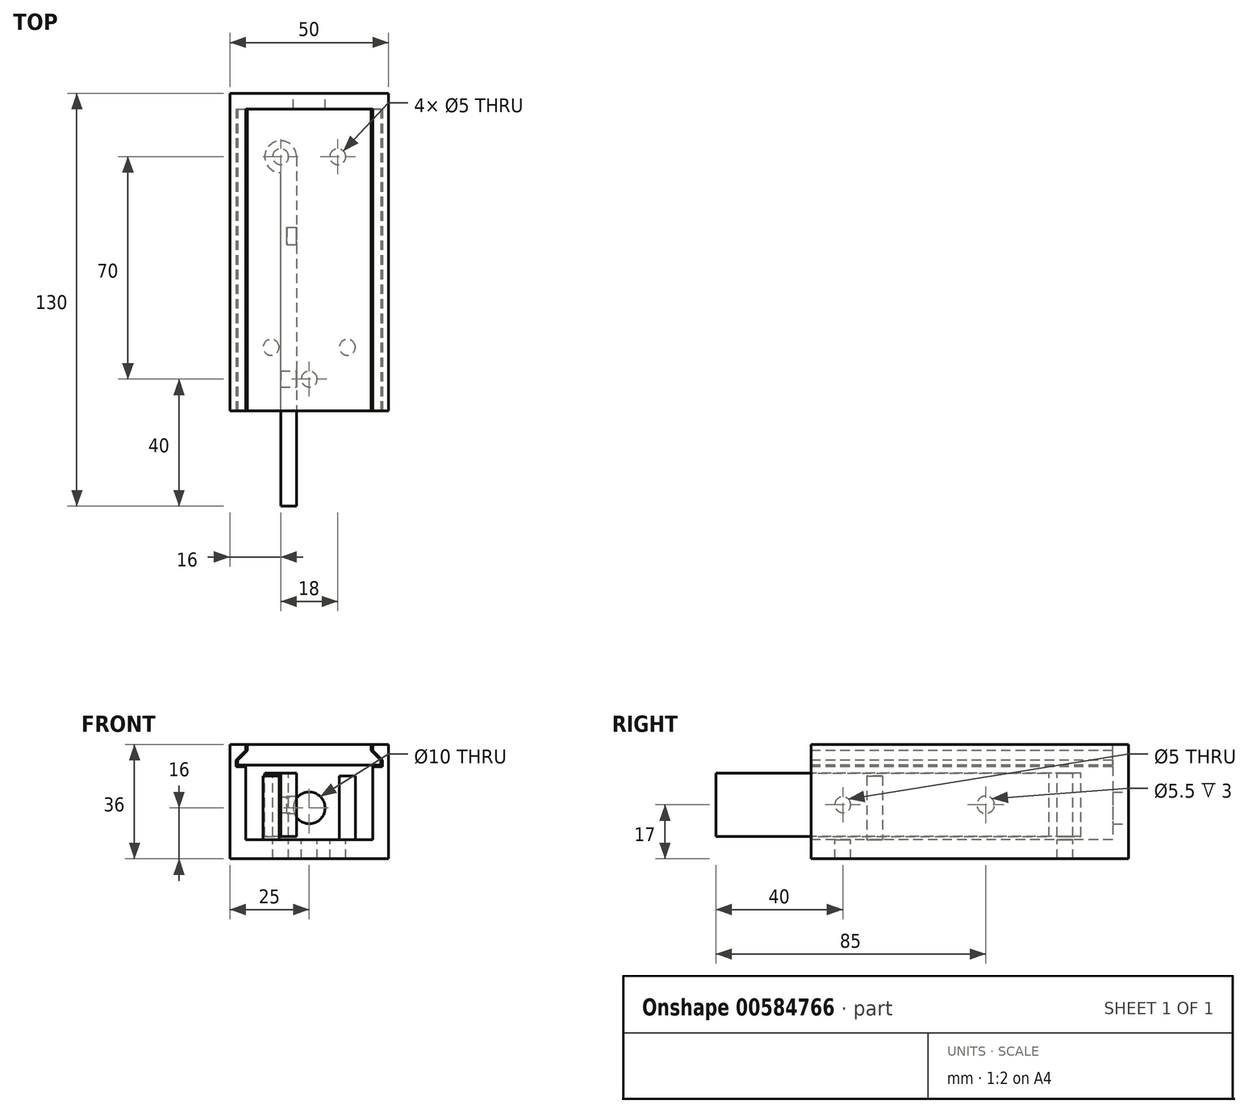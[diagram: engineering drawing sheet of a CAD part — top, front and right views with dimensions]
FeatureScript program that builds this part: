
annotation { "Feature Type Name" : "Feature", "Feature Type Description" : "" }
export const myFeature = defineFeature(function(context is Context, id is Id, definition is map)
    precondition{}
    {
        {
            var Q0;
            Q0=qCreatedBy(makeId("Top.planeOp"),FACE);
            var sketch = newSketch(context, id + "F0", { "sketchPlane" : qUnion([Q0])});
            skLineSegment(sketch, "E0.bottom", {"start": v(25, 50) * mm, "end": v(-25, 50) * mm});
            skLineSegment(sketch, "E0.top", {"start": v(25, -50) * mm, "end": v(-25, -50) * mm});
            skLineSegment(sketch, "E0.left", {"start": v(25, 50) * mm, "end": v(25, -50) * mm});
            skLineSegment(sketch, "E0.right", {"start": v(-25, 50) * mm, "end": v(-25, -50) * mm});
            skPoint(sketch, "E0.middle", {"position": v(0, 0) * mm});
            skSolve(sketch);
        }
        {
            var Q0;
            Q0=makeQuery(id+"F0.imprint","IMPRINT",FACE,{"disambiguationData":[TD([[makeQuery(id+"F0.imprint","IMPRINT",EDGE,{"derivedFrom":sQuery(id+"F0.wireOp",EDGE,"E0.bottom")}),1.0]])]});
            extrude(context, id + "F1", {"entities" : qUnion([Q0]), "depth" : 6 * mm, "offsetDistance" : 25 * mm});
        }
        {
            var Q0;
            Q0=makeQuery(id+"F1.opExtrude","CAP_FACE",FACE,{"disambiguationData":[OSD([sQuery(id+"F0.wireOp",EDGE,"E0.bottom"),sQuery(id+"F0.wireOp",EDGE,"E0.top"),sQuery(id+"F0.wireOp",EDGE,"E0.left"),sQuery(id+"F0.wireOp",EDGE,"E0.right")])],"isStart":false});
            var sketch = newSketch(context, id + "F2", { "sketchPlane" : qUnion([Q0])});
            skLineSegment(sketch, "E1.bottom", {"start": v(-25, 50) * mm, "end": v(-20, 50) * mm});
            skLineSegment(sketch, "E1.top", {"start": v(-25, -50) * mm, "end": v(-20, -50) * mm});
            skLineSegment(sketch, "E1.left", {"start": v(-25, 50) * mm, "end": v(-25, -50) * mm});
            skLineSegment(sketch, "E1.right", {"start": v(-20, 45) * mm, "end": v(-20, -50) * mm});
            skLineSegment(sketch, "E2.bottom", {"start": v(-25, 50) * mm, "end": v(25, 50) * mm});
            skLineSegment(sketch, "E2.top", {"start": v(-20, 45) * mm, "end": v(20, 45) * mm});
            skLineSegment(sketch, "E2.left", {"start": v(-25, 50) * mm, "end": v(-25, 45) * mm});
            skLineSegment(sketch, "E2.right", {"start": v(25, 50) * mm, "end": v(25, 45) * mm});
            skLineSegment(sketch, "E3.bottom", {"start": v(25, 50) * mm, "end": v(20, 50) * mm});
            skLineSegment(sketch, "E3.top", {"start": v(25, -50) * mm, "end": v(20, -50) * mm});
            skLineSegment(sketch, "E3.left", {"start": v(25, 50) * mm, "end": v(25, -50) * mm});
            skLineSegment(sketch, "E3.right", {"start": v(20, 45) * mm, "end": v(20, -50) * mm});
            skLineSegment(sketch, "E4.bottom", {"start": v(-2, -50) * mm, "end": v(2, -50) * mm});
            skLineSegment(sketch, "E4.top", {"start": v(-2, -45) * mm, "end": v(2, -45) * mm});
            skLineSegment(sketch, "E4.left", {"start": v(-2, -50) * mm, "end": v(-2, -45) * mm});
            skLineSegment(sketch, "E4.right", {"start": v(2, -50) * mm, "end": v(2, -45) * mm});
            skPoint(sketch, "E5", {"position": v(0, -45) * mm});
            skSolve(sketch);
        }
        {
            var Q0;
            Q0=makeQuery(id+"F2.imprint","IMPRINT",FACE,{"disambiguationData":[TD([[makeQuery(id+"F2.imprint","IMPRINT",EDGE,{"derivedFrom":sQuery(id+"F2.wireOp",EDGE,"E1.top")}),-1.0]])]});
            extrude(context, id + "F3", {"entities" : qUnion([Q0]), "operationType" : NewBodyOperationType.ADD, "depth" : 30 * mm, "offsetDistance" : 25 * mm});
        }
        {
            var Q0;
            Q0=makeQuery(id+"F3.boolean.opBoolean","MERGE",FACE,{"derivedFrom":[makeQuery(id+"F1.opExtrude","SWEPT_FACE",FACE,{"disambiguationData":[OSD([sQuery(id+"F0.wireOp",EDGE,"E0.top")])]}),makeQuery(id+"F3.opExtrude","SWEPT_FACE",FACE,{"disambiguationData":[OSD([sQuery(id+"F2.wireOp",EDGE,"E1.top")])]}),makeQuery(id+"F3.opExtrude","SWEPT_FACE",FACE,{"disambiguationData":[OSD([sQuery(id+"F2.wireOp",EDGE,"E3.top")])]})]});
            var sketch = newSketch(context, id + "F4", { "sketchPlane" : qUnion([Q0])});
            skLineSegment(sketch, "E6", {"start": v(-20, 29) * mm, "end": v(-23, 29) * mm});
            skLineSegment(sketch, "E7", {"start": v(-23, 29) * mm, "end": v(-23, 31) * mm});
            skLineSegment(sketch, "E8", {"start": v(0, 0) * mm, "end": v(0, 6) * mm});
            skLineSegment(sketch, "E9.MirrorCS", {"start": v(23, 29) * mm, "end": v(23, 31) * mm});
            skLineSegment(sketch, "E10.MirrorCS", {"start": v(23, 31) * mm, "end": v(20, 34) * mm});
            skLineSegment(sketch, "E11.MirrorCS", {"start": v(20, 29) * mm, "end": v(23, 29) * mm});
            skLineSegment(sketch, "E12", {"start": v(-23, 31) * mm, "end": v(-20, 34) * mm});
            skSolve(sketch);
        }
        {
            var Q0;
            {var subQ0=sQuery(id+"F4.wireOp",EDGE,"E6");Q0=makeQuery(id+"F4.imprint","IMPRINT",FACE,{"disambiguationData":[TD([[makeQuery(id+"F4.imprint","IMPRINT",EDGE,{"derivedFrom":subQ0}),-1.0]])]});}
            var Q1;
            Q1=makeQuery(id+"F4.imprint","IMPRINT",FACE,{"disambiguationData":[TD([[makeQuery(id+"F4.imprint","IMPRINT",EDGE,{"derivedFrom":sQuery(id+"F4.wireOp",EDGE,"E9.MirrorCS")}),1.0]])]});
            extrude(context, id + "F5", {"entities" : qUnion([Q0, Q1]), "operationType" : NewBodyOperationType.REMOVE, "oppositeDirection" : true, "depth" : 95 * mm, "offsetDistance" : 25 * mm});
        }
        {
            var Q0;
            Q0=qCreatedBy(makeId("Front.planeOp"),FACE);
            cPlane(context, id + "F6", {"entities" : qUnion([Q0]), "cplaneType" : CPlaneType.OFFSET, "offset" : 50 * mm, "width" : 150 * mm, "height" : 150 * mm});
        }
        {
            var Q0;
            Q0=qCreatedBy(id+"F6.planeOp",FACE);
            var sketch = newSketch(context, id + "F7", { "sketchPlane" : qUnion([Q0])});
            skLineSegment(sketch, "E13.0", {"start": v(-20, 29) * mm, "end": v(-23, 29) * mm});
            skLineSegment(sketch, "E14.0", {"start": v(-20, 29) * mm, "end": v(-20, 6) * mm});
            skLineSegment(sketch, "E15.0", {"start": v(20, 29) * mm, "end": v(20, 6) * mm});
            skLineSegment(sketch, "E16.top", {"start": v(-22.5, 29.5) * mm, "end": v(22.5, 29.5) * mm});
            skLineSegment(sketch, "E16.left", {"start": v(-22.5, 31) * mm, "end": v(-22.5, 29.5) * mm});
            skLineSegment(sketch, "E16.right", {"start": v(22.5, 31) * mm, "end": v(22.5, 29.5) * mm});
            skLineSegment(sketch, "E17.top", {"start": v(-19.5, 36) * mm, "end": v(19.5, 36) * mm});
            skLineSegment(sketch, "E17.left", {"start": v(-19.5, 34) * mm, "end": v(-19.5, 36) * mm});
            skLineSegment(sketch, "E17.right", {"start": v(19.5, 34) * mm, "end": v(19.5, 36) * mm});
            skLineSegment(sketch, "E18.0", {"start": v(-23, 29) * mm, "end": v(-23, 31) * mm});
            skLineSegment(sketch, "E19.0", {"start": v(-23, 31) * mm, "end": v(-20, 34) * mm});
            skLineSegment(sketch, "E20.0", {"start": v(-20, 36) * mm, "end": v(-20, 34) * mm});
            skLineSegment(sketch, "E21", {"start": v(-22.5, 31) * mm, "end": v(-19.5, 34) * mm});
            skLineSegment(sketch, "E22.0", {"start": v(23, 31) * mm, "end": v(20, 34) * mm});
            skLineSegment(sketch, "E23.0", {"start": v(20, 36) * mm, "end": v(20, 34) * mm});
            skLineSegment(sketch, "E24.0", {"start": v(23, 29) * mm, "end": v(23, 31) * mm});
            skLineSegment(sketch, "E25.0", {"start": v(20, 29) * mm, "end": v(23, 29) * mm});
            skLineSegment(sketch, "E26", {"start": v(22.5, 31) * mm, "end": v(19.5, 34) * mm});
            skSolve(sketch);
        }
        {
            var Q0;
            Q0=makeQuery(id+"F1.opExtrude","CAP_FACE",FACE,{"disambiguationData":[OSD([sQuery(id+"F0.wireOp",EDGE,"E0.bottom"),sQuery(id+"F0.wireOp",EDGE,"E0.top"),sQuery(id+"F0.wireOp",EDGE,"E0.left"),sQuery(id+"F0.wireOp",EDGE,"E0.right")])],"isStart":false});
            var sketch = newSketch(context, id + "F8", { "sketchPlane" : qUnion([Q0])});
            skCircle(sketch, "E27", {"center": v(-9, 30) * mm, "radius": 2.5 * mm});
            skLineSegment(sketch, "E28", {"start": v(-9, 30) * mm, "end": v(-20, 30) * mm, "construction": true});
            skCircle(sketch, "E29", {"center": v(9, 30) * mm, "radius": 2.5 * mm});
            skLineSegment(sketch, "E30", {"start": v(9, 30) * mm, "end": v(20, 30) * mm, "construction": true});
            skLineSegment(sketch, "E31", {"start": v(-9, 30) * mm, "end": v(9, 30) * mm, "construction": true});
            skCircle(sketch, "E32", {"center": v(0, -40) * mm, "radius": 2.5 * mm});
            skLineSegment(sketch, "E33", {"start": v(0, -40) * mm, "end": v(-20, -40) * mm, "construction": true});
            skLineSegment(sketch, "E34", {"start": v(0, -40) * mm, "end": v(20, -40) * mm, "construction": true});
            skCircle(sketch, "E35", {"center": v(-12, -30) * mm, "radius": 2.5 * mm});
            skCircle(sketch, "E36", {"center": v(12, -30) * mm, "radius": 2.5 * mm});
            skLineSegment(sketch, "E37", {"start": v(-12, -30) * mm, "end": v(-20, -30) * mm, "construction": true});
            skLineSegment(sketch, "E38", {"start": v(12, -30) * mm, "end": v(20, -30) * mm, "construction": true});
            skSolve(sketch);
        }
        {
            var Q0;
            Q0=makeQuery(id+"F8.imprint","IMPRINT",FACE,{"disambiguationData":[TD([[makeQuery(id+"F8.imprint","IMPRINT",EDGE,{"derivedFrom":sQuery(id+"F8.wireOp",EDGE,"E32")}),1.0]])]});
            var Q1;
            Q1=makeQuery(id+"F8.imprint","IMPRINT",FACE,{"disambiguationData":[TD([[makeQuery(id+"F8.imprint","IMPRINT",EDGE,{"derivedFrom":sQuery(id+"F8.wireOp",EDGE,"E27")}),1.0]])]});
            var Q2;
            Q2=makeQuery(id+"F8.imprint","IMPRINT",FACE,{"disambiguationData":[TD([[makeQuery(id+"F8.imprint","IMPRINT",EDGE,{"derivedFrom":sQuery(id+"F8.wireOp",EDGE,"E29")}),1.0]])]});
            extrude(context, id + "F9", {"entities" : qUnion([Q0, Q1, Q2]), "operationType" : NewBodyOperationType.REMOVE, "endBound" : BoundingType.UP_TO_NEXT, "oppositeDirection" : true, "depth" : 25 * mm, "offsetDistance" : 25 * mm});
        }
        {
            var Q0;
            Q0=makeQuery(id+"F3.boolean.opBoolean","MERGE",FACE,{"derivedFrom":[makeQuery(id+"F1.opExtrude","SWEPT_FACE",FACE,{"disambiguationData":[OSD([sQuery(id+"F0.wireOp",EDGE,"E0.bottom")])]}),makeQuery(id+"F3.opExtrude","SWEPT_FACE",FACE,{"disambiguationData":[OSD([sQuery(id+"F2.wireOp",EDGE,"E2.bottom"),sQuery(id+"F2.wireOp",EDGE,"E3.bottom")])]})]});
            var sketch = newSketch(context, id + "F10", { "sketchPlane" : qUnion([Q0])});
            skCircle(sketch, "E39", {"center": v(0, 16) * mm, "radius": 5 * mm});
            skLineSegment(sketch, "E40.0", {"start": v(20, 6) * mm, "end": v(-20, 6) * mm});
            skSolve(sketch);
        }
        {
            var Q0;
            Q0=makeQuery(id+"F10.imprint","IMPRINT",FACE,{"disambiguationData":[TD([[makeQuery(id+"F10.imprint","IMPRINT",EDGE,{"derivedFrom":sQuery(id+"F10.wireOp",EDGE,"E39")}),1.0]])]});
            extrude(context, id + "F11", {"entities" : qUnion([Q0]), "operationType" : NewBodyOperationType.REMOVE, "endBound" : BoundingType.UP_TO_NEXT, "oppositeDirection" : true, "depth" : 25 * mm, "offsetDistance" : 25 * mm});
        }
        {
            var Q0;
            Q0=makeQuery(id+"F7.imprint","IMPRINT",FACE,{"disambiguationData":[TD([[makeQuery(id+"F7.imprint","IMPRINT",EDGE,{"derivedFrom":sQuery(id+"F7.wireOp",EDGE,"E16.top")}),1.0]])]});
            extrude(context, id + "F12", {"entities" : qUnion([Q0]), "oppositeDirection" : true, "depth" : 95 * mm, "offsetDistance" : 25 * mm});
        }
        {
            var Q0;
            Q0=qCreatedBy(makeId("Top.planeOp"),FACE);
            cPlane(context, id + "F13", {"entities" : qUnion([Q0]), "cplaneType" : CPlaneType.OFFSET, "offset" : 27 * mm, "width" : 150 * mm, "height" : 150 * mm});
        }
        {
            var Q0;
            Q0=qCreatedBy(id+"F13.planeOp",FACE);
            var sketch = newSketch(context, id + "F14", { "sketchPlane" : qUnion([Q0])});
            skCircle(sketch, "E41.0", {"center": v(-9, 30) * mm, "radius": 2.5 * mm});
            skArc(sketch, "E42", {"start": v(-4, 30) * mm, "mid": v(-12.54, 33.54) * mm, "end": v(-9, 25) * mm});
            skLineSegment(sketch, "E43", {"start": v(-4, 30) * mm, "end": v(-4, -80) * mm});
            skLineSegment(sketch, "E44", {"start": v(-4, -80) * mm, "end": v(-9, -80) * mm});
            skLineSegment(sketch, "E45", {"start": v(-9, -80) * mm, "end": v(-9, 25) * mm});
            skSolve(sketch);
        }
        {
            var Q0;
            Q0=makeQuery(id+"F14.imprint","IMPRINT",FACE,{"disambiguationData":[TD([[makeQuery(id+"F14.imprint","IMPRINT",EDGE,{"derivedFrom":sQuery(id+"F14.wireOp",EDGE,"E41.0")}),-1.0]])]});
            var Q1;
            Q1=makeQuery(id+"F14.imprint","IMPRINT",FACE,{"disambiguationData":[TD([[makeQuery(id+"F14.imprint","IMPRINT",EDGE,{"derivedFrom":sQuery(id+"F14.wireOp",EDGE,"bdc069c4-55b5-4009-95dd-62438d2669f5.0")}),-1.0]])]});
            extrude(context, id + "F15", {"entities" : qUnion([Q0, Q1]), "oppositeDirection" : true, "depth" : 20 * mm, "offsetDistance" : 25 * mm});
        }
        {
            var Q0;
            Q0=makeQuery(id+"F15.opExtrude","SWEPT_FACE",FACE,{"disambiguationData":[OSD([sQuery(id+"F14.wireOp",EDGE,"E43")])]});
            var sketch = newSketch(context, id + "F16", { "sketchPlane" : qUnion([Q0])});
            skCircle(sketch, "E46", {"center": v(-40, 17) * mm, "radius": 2.5 * mm});
            skPoint(sketch, "E47", {"position": v(30, 17) * mm});
            skCircle(sketch, "E48", {"center": v(5, 17) * mm, "radius": 2.75 * mm});
            skSolve(sketch);
        }
        {
            var Q0;
            Q0=makeQuery(id+"F16.imprint","IMPRINT",FACE,{"disambiguationData":[TD([[makeQuery(id+"F16.imprint","IMPRINT",EDGE,{"derivedFrom":sQuery(id+"F16.wireOp",EDGE,"E46")}),1.0]])]});
            extrude(context, id + "F17", {"entities" : qUnion([Q0]), "operationType" : NewBodyOperationType.REMOVE, "endBound" : BoundingType.UP_TO_NEXT, "oppositeDirection" : true, "depth" : 25 * mm, "offsetDistance" : 25 * mm});
        }
        {
            var Q0;
            Q0=makeQuery(id+"F16.imprint","IMPRINT",FACE,{"disambiguationData":[TD([[makeQuery(id+"F16.imprint","IMPRINT",EDGE,{"derivedFrom":sQuery(id+"F16.wireOp",EDGE,"E48")}),1.0]])]});
            extrude(context, id + "F18", {"entities" : qUnion([Q0]), "operationType" : NewBodyOperationType.REMOVE, "oppositeDirection" : true, "depth" : 3 * mm, "offsetDistance" : 25 * mm});
        }
        {
            var Q0;
            Q0=makeQuery(id+"F8.imprint","IMPRINT",FACE,{"disambiguationData":[TD([[makeQuery(id+"F8.imprint","IMPRINT",EDGE,{"derivedFrom":sQuery(id+"F8.wireOp",EDGE,"E35")}),1.0]])]});
            var Q1;
            Q1=makeQuery(id+"F8.imprint","IMPRINT",FACE,{"disambiguationData":[TD([[makeQuery(id+"F8.imprint","IMPRINT",EDGE,{"derivedFrom":sQuery(id+"F8.wireOp",EDGE,"E36")}),1.0]])]});
            extrude(context, id + "F19", {"entities" : qUnion([Q0, Q1]), "operationType" : NewBodyOperationType.ADD, "depth" : 20 * mm, "offsetDistance" : 25 * mm});
        }
    });
